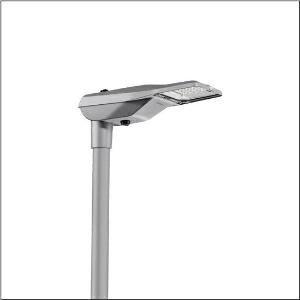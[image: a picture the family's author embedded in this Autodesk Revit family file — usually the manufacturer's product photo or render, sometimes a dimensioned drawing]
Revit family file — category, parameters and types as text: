
# Revit family: streetlight_sl_21_iq_micro___st1_0a_5xe1d51y08db_19c1
name_source: partatom
category: Lighting Fixtures
units: mm (PartAtom-declared; Revit-internal decimal feet)

## family parameters
Cut with Voids When Loaded = No
Host = Face
Light Source = No
Part Type = Normal
Room Calculation Point = No
Round Connector Dimension = Use Diameter
Shared = No

## types (1)
- --- (1 x LED, 4490 lm, 39.1 W, 3000K)
    Apparent Load = 39 VA
    CIE Flux Codes = 37 72 97 100 100
    Color Rendering = 80
    Color Temperature = 3000K
    Default Elevation = 1800 mm
    Description = Streetlight SL 21 iQ micro, mast luminaire, primary light control with lens, of PMMA, primary optical cover: cover, of toughened safety glass, transparent, light distribution: ST1.0a, light emission: direct distribution, primary light characteristic: asymmetric, installation type: post-top, side-entry, LED, High Power LED, rated luminous flux: 4.490lm, luminous efficacy: 115lm/W, light colour: 830, colour temperature: 3000K, control: presetting dimming logarithmic, Street-Remote, Auto-Match, Temp-Guard, Lumen-Switch, Night-Set, Smart-Wire, Light-Fading, Desk-Remote (wireless, voltage-free reading and setting of iQ features in the workshop via application-optimized NFC function/RFID function), optimised constant luminous flux control (CLO 2.0), mains connection: 220..240V, AC, 50/60Hz, start of lifetime: 39W, end of service life: 41W, reduction: 17W, luminaire housing, of diecast aluminium, powder-coated, Siteco® metallic grey (DB 702S), corrosivity category C5 mid according to DIN EN ISO 12944, please order mast flange separately, inclination adjustable: 0°, 5°, 10°, 15°, sealing non-destructively replaceable, multi-level sealing system, length: 528mm, width: 235mm, height: 110mm, mast flange for spigot size: 42mm (side-entry): 5XC10008XM4, 60/48mm (side-entry/post-top): 5XC10108XM2, 76/60mm (side-entry/post-top): 5XC10108XM1, Smart Interface below and above, protection rating (complete): IP66, insulation class (complete): insulation class II (safety insulation), certification: CE, ENEC, ENEC+, VDE, impact resistance: IK09, permissible operating ambient temperature for outdoor applications: -40..+50°C, standard-compliant lighting for roads and squares, packaging unit: 1 piece

Light Distribution: ST1.0a
    Height = 110 mm
    Lamp = 1 x LED
    Lamp Light Flux = 4490 lm
    Lamp Power = 39.1 W
    Lamp count = 1
    Length = 528 mm
    Luminous efficacy = 115 lm/W
    Manufacturer = Siteco
    ModVariant = No
    Model = 5XE1D51Y08DB
    Number of Poles = 1
    OnlyDefault = Yes
    Power Factor = 1
    Product Name = Streetlight SL 21 iQ micro | ST1.0a
    Product group = mast luminaire | pylon top
    ProductGroupID = 6100
    Protection Class = Protection class II
    Protection Degree = IP 66
    RLX_Detail_Level = 1
    RLX_Emergency_Light_Flux = 0 lm
    RLX_Emergency_Type = 0
    RLX_Emergency_Type_DB = No
    RlxData = <blob elided: 98657 chars, md5=778de8dc>
    Socket = socket
    Standby Power = 0 W
    System Light Flux = 4490 lm
    System Power = 39 W
    Type Comments = factory setting: luminous flux: 100 % | dim-lin: 254 | 765 mA
    Type Image = l_1007239.jpg
    URL = http://relux.com
    VarID = @adj_045381
    Voltage = 0 V
    Weight = 0.00 kg
    Width = 235 mm

## geometry (parser evidence)
native form markers: Blend x4, Sweep x11
no freeform markers — native parametric forms only
